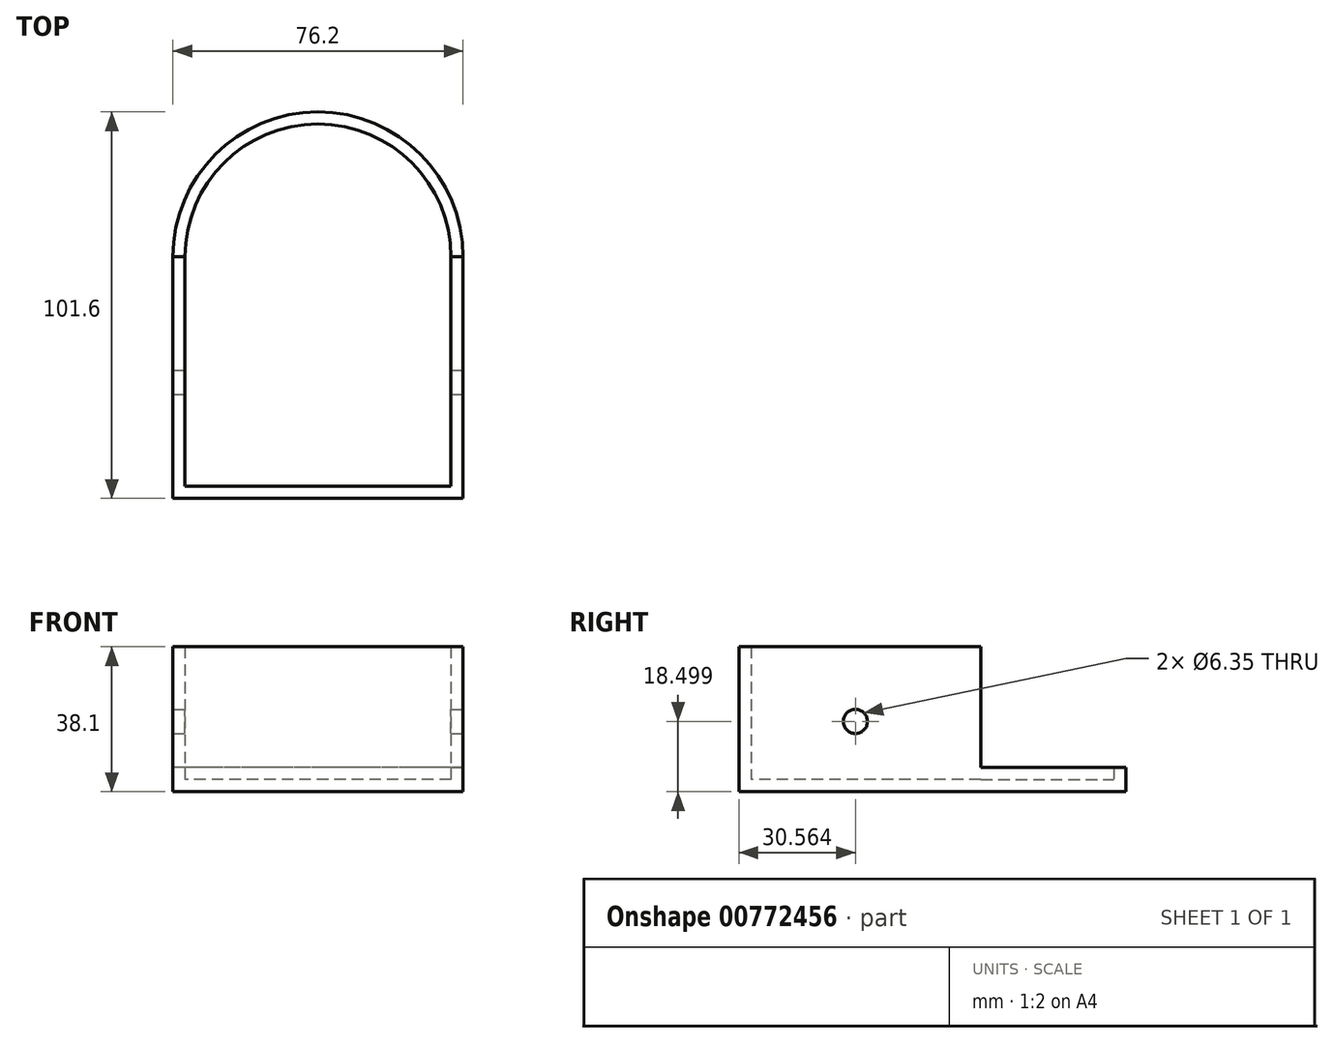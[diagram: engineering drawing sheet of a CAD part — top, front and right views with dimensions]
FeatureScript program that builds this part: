
annotation { "Feature Type Name" : "Feature", "Feature Type Description" : "" }
export const myFeature = defineFeature(function(context is Context, id is Id, definition is map)
    precondition{}
    {
        {
            var Q0;
            Q0=qCreatedBy(makeId("Top.planeOp"),FACE);
            var sketch = newSketch(context, id + "F0", { "sketchPlane" : qUnion([Q0])});
            skArc(sketch, "E0", {"start": v(38.1, 0) * mm, "mid": v(0, 38.1) * mm, "end": v(-38.1, 0) * mm});
            skLineSegment(sketch, "E1", {"start": v(-38.1, 0) * mm, "end": v(-38.1, -63.5) * mm});
            skLineSegment(sketch, "E2", {"start": v(38.1, 0) * mm, "end": v(38.1, -63.5) * mm});
            skLineSegment(sketch, "E3", {"start": v(38.1, -63.5) * mm, "end": v(-38.1, -63.5) * mm});
            skArc(sketch, "E4.0", {"start": v(34.93, 0) * mm, "mid": v(0, 34.93) * mm, "end": v(-34.93, 0) * mm});
            skLineSegment(sketch, "E5.0", {"start": v(34.93, 0) * mm, "end": v(34.93, -60.32) * mm});
            skLineSegment(sketch, "E5.1", {"start": v(34.93, -60.32) * mm, "end": v(-34.93, -60.32) * mm});
            skLineSegment(sketch, "E5.2", {"start": v(-34.93, 0) * mm, "end": v(-34.93, -60.32) * mm});
            skLineSegment(sketch, "E6", {"start": v(-34.93, 0) * mm, "end": v(-38.1, 0) * mm});
            skLineSegment(sketch, "E7", {"start": v(34.93, 0) * mm, "end": v(38.1, 0) * mm});
            skLineSegment(sketch, "E8", {"start": v(-34.93, -60.32) * mm, "end": v(-38.1, -60.32) * mm});
            skLineSegment(sketch, "E9", {"start": v(34.93, -60.32) * mm, "end": v(38.1, -60.32) * mm});
            skSolve(sketch);
        }
        {
            var Q0;
            Q0=makeQuery(id+"F0.imprint","IMPRINT",FACE,{"disambiguationData":[TD([[makeQuery(id+"F0.imprint","IMPRINT",EDGE,{"derivedFrom":sQuery(id+"F0.wireOp",EDGE,"E4.0")}),1.0]])]});
            extrude(context, id + "F1", {"entities" : qUnion([Q0]), "depth" : 3.17 * mm, "offsetDistance" : 25.4 * mm});
        }
        {
            var Q0;
            Q0=makeQuery(id+"F0.imprint","IMPRINT",FACE,{"disambiguationData":[TD([[makeQuery(id+"F0.imprint","IMPRINT",EDGE,{"derivedFrom":sQuery(id+"F0.wireOp",EDGE,"E0")}),1.0]])]});
            extrude(context, id + "F2", {"entities" : qUnion([Q0]), "operationType" : NewBodyOperationType.ADD, "depth" : 6.35 * mm, "offsetDistance" : 25.4 * mm});
        }
        {
            var Q0;
            {var subQ0=sQuery(id+"F0.wireOp",EDGE,"E3");Q0=makeQuery(id+"F0.imprint","IMPRINT",FACE,{"disambiguationData":[TD([[makeQuery(id+"F0.imprint","IMPRINT",EDGE,{"derivedFrom":subQ0}),-1.0]])]});}
            extrude(context, id + "F3", {"entities" : qUnion([Q0]), "operationType" : NewBodyOperationType.ADD, "depth" : 38.1 * mm, "offsetDistance" : 25.4 * mm});
        }
        {
            var Q0;
            Q0=makeQuery(id+"F0.imprint","IMPRINT",FACE,{"disambiguationData":[TD([[makeQuery(id+"F0.imprint","IMPRINT",EDGE,{"derivedFrom":sQuery(id+"F0.wireOp",EDGE,"E5.2")}),-1.0]])]});
            extrude(context, id + "F4", {"entities" : qUnion([Q0]), "operationType" : NewBodyOperationType.ADD, "depth" : 38.1 * mm, "offsetDistance" : 25.4 * mm});
        }
        {
            var Q0;
            Q0=makeQuery(id+"F0.imprint","IMPRINT",FACE,{"disambiguationData":[TD([[makeQuery(id+"F0.imprint","IMPRINT",EDGE,{"derivedFrom":sQuery(id+"F0.wireOp",EDGE,"E5.0")}),1.0]])]});
            extrude(context, id + "F5", {"entities" : qUnion([Q0]), "operationType" : NewBodyOperationType.ADD, "depth" : 38.1 * mm, "offsetDistance" : 25.4 * mm});
        }
        {
            var Q0;
            {var subQ0=sQuery(id+"F0.wireOp",EDGE,"E2");Q0=makeQuery(id+"F5.boolean.opBoolean","MERGE",FACE,{"derivedFrom":[makeQuery(id+"F3.opExtrude","SWEPT_FACE",FACE,{"disambiguationData":[OSD([subQ0])]}),makeQuery(id+"F5.opExtrude","SWEPT_FACE",FACE,{"disambiguationData":[OSD([subQ0])]})]});}
            var sketch = newSketch(context, id + "F6", { "sketchPlane" : qUnion([Q0])});
            skCircle(sketch, "E10", {"center": v(-32.94, 18.5) * mm, "radius": 3.18 * mm});
            skSolve(sketch);
        }
        {
            var Q0;
            Q0=makeQuery(id+"F6.imprint","IMPRINT",FACE,{"disambiguationData":[TD([[makeQuery(id+"F6.imprint","IMPRINT",EDGE,{"derivedFrom":sQuery(id+"F6.wireOp",EDGE,"E10")}),1.0]])]});
            extrude(context, id + "F7", {"entities" : qUnion([Q0]), "operationType" : NewBodyOperationType.REMOVE, "oppositeDirection" : true, "depth" : 76.2 * mm, "offsetDistance" : 25.4 * mm});
        }
    });
